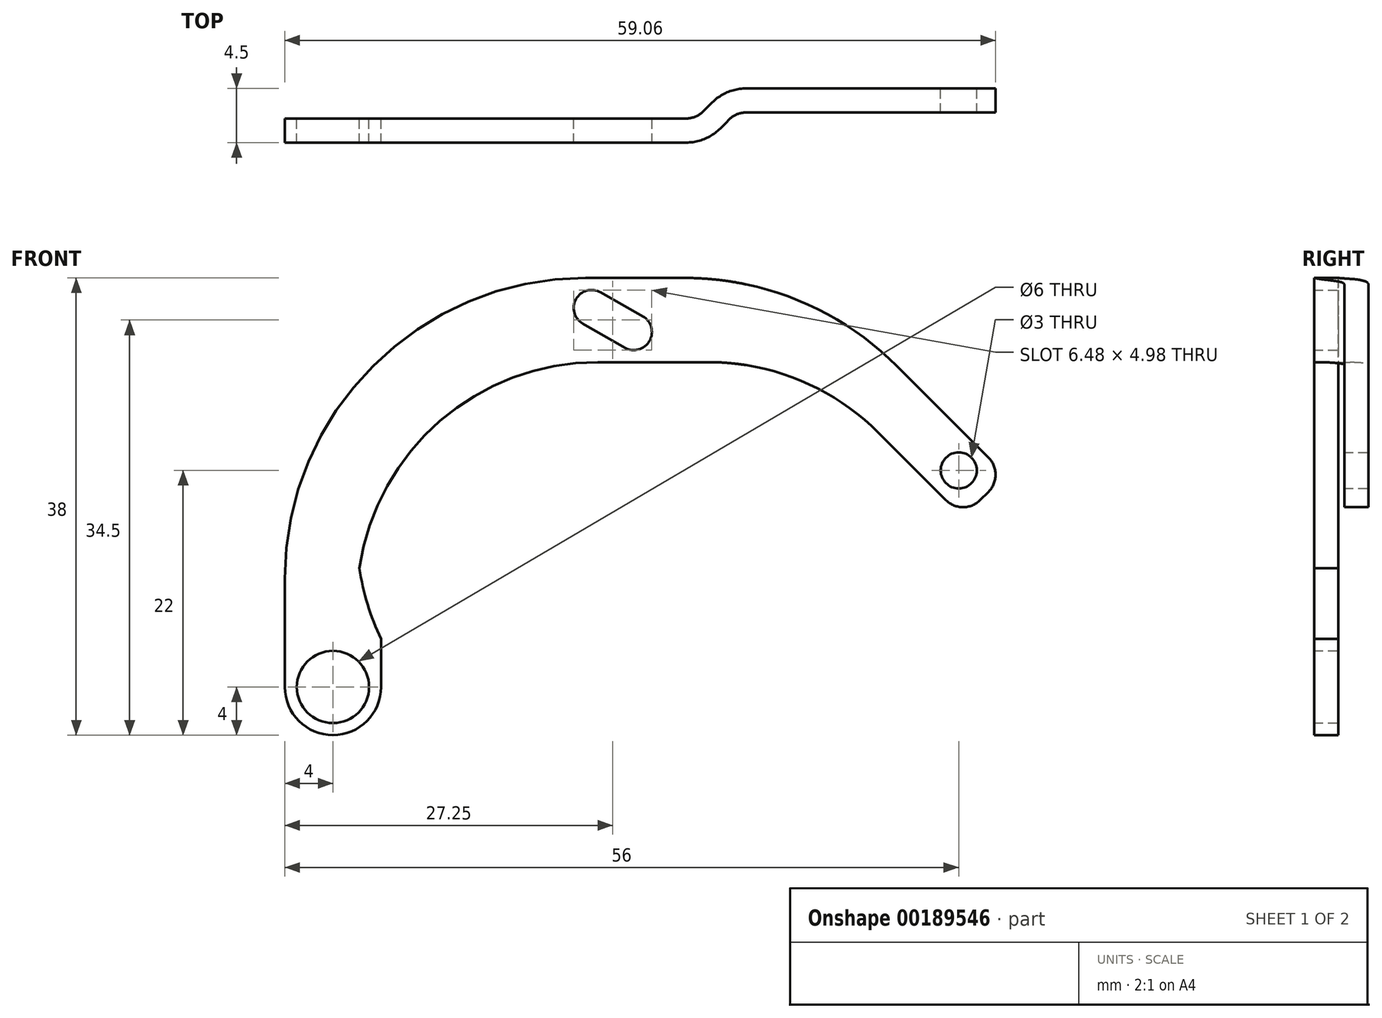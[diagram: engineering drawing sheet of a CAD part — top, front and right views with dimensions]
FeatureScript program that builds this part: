
annotation { "Feature Type Name" : "Feature", "Feature Type Description" : "" }
export const myFeature = defineFeature(function(context is Context, id is Id, definition is map)
    precondition{}
    {
        {
            var Q0;
            Q0=qCreatedBy(makeId("Front.planeOp"),FACE);
            var sketch = newSketch(context, id + "F0", { "sketchPlane" : qUnion([Q0])});
            skCircle(sketch, "E0", {"center": v(0, 0) * mm, "radius": 3 * mm});
            skArc(sketch, "E1", {"start": v(24.26, 28.2) * mm, "mid": v(26.3, 28.76) * mm, "end": v(25.74, 30.8) * mm});
            skLineSegment(sketch, "E2.bottom", {"start": v(-4, -4) * mm, "end": v(4, -4) * mm});
            skLineSegment(sketch, "E2.top", {"start": v(-4, 27) * mm, "end": v(4, 27) * mm});
            skLineSegment(sketch, "E2.left", {"start": v(-4, -4) * mm, "end": v(-4, 27) * mm});
            skLineSegment(sketch, "E2.right", {"start": v(4, -4) * mm, "end": v(4, 27) * mm});
            skLineSegment(sketch, "E3.bottom", {"start": v(-4, 27) * mm, "end": v(39.46, 27) * mm});
            skLineSegment(sketch, "E3.top", {"start": v(-4, 34) * mm, "end": v(39.54, 34) * mm});
            skLineSegment(sketch, "E3.left", {"start": v(-4, 27) * mm, "end": v(-4, 34) * mm});
            skCircle(sketch, "E4", {"center": v(52, 18) * mm, "radius": 1.5 * mm});
            skLineSegment(sketch, "E5.left", {"start": v(52.35, 14.11) * mm, "end": v(39.46, 27) * mm});
            skLineSegment(sketch, "E5.right", {"start": v(55.89, 17.65) * mm, "end": v(39.54, 34) * mm});
            skLineSegment(sketch, "E6.bottom", {"start": v(4, 27) * mm, "end": v(2, 27) * mm});
            skLineSegment(sketch, "E6.top", {"start": v(4, 4) * mm, "end": v(2, 4) * mm});
            skLineSegment(sketch, "E6.left", {"start": v(4, 27) * mm, "end": v(4, 4) * mm});
            skLineSegment(sketch, "E6.right", {"start": v(2, 27) * mm, "end": v(2, 4) * mm});
            skArc(sketch, "E7", {"start": v(22.24, 32.8) * mm, "mid": v(20.2, 32.24) * mm, "end": v(20.76, 30.2) * mm});
            skLineSegment(sketch, "E8", {"start": v(22.24, 32.8) * mm, "end": v(25.74, 30.8) * mm});
            skLineSegment(sketch, "E9", {"start": v(24.26, 28.2) * mm, "end": v(20.76, 30.2) * mm});
            skLineSegment(sketch, "E10", {"start": v(52.35, 14.11) * mm, "end": v(55.89, 17.65) * mm});
            skSolve(sketch);
        }
        {
            var Q0;
            Q0=makeQuery(id+"F0.imprint","IMPRINT",FACE,{"disambiguationData":[TD([[makeQuery(id+"F0.imprint","IMPRINT",EDGE,{"derivedFrom":sQuery(id+"F0.wireOp",EDGE,"E0")}),-1.0]])]});
            var Q1;
            Q1=makeQuery(id+"F0.imprint","IMPRINT",FACE,{"disambiguationData":[TD([[makeQuery(id+"F0.imprint","IMPRINT",EDGE,{"derivedFrom":sQuery(id+"F0.wireOp",EDGE,"E1")}),-1.0]])]});
            var Q2;
            Q2=makeQuery(id+"F0.imprint","IMPRINT",FACE,{"disambiguationData":[TD([[makeQuery(id+"F0.imprint","IMPRINT",EDGE,{"derivedFrom":sQuery(id+"F0.wireOp",EDGE,"J9uZ1ApI-m34T-gY4W-De5X-UlzJvXiWbMHB.bottom")}),-1.0]])]});
            var Q3;
            Q3=makeQuery(id+"F0.imprint","IMPRINT",FACE,{"disambiguationData":[TD([[makeQuery(id+"F0.imprint","IMPRINT",EDGE,{"derivedFrom":sQuery(id+"F0.wireOp",EDGE,"E4")}),-1.0]])]});
            extrude(context, id + "F1", {"entities" : qUnion([Q0, Q1, Q2, Q3]), "depth" : 4.5 * mm});
        }
        {
            var Q0;
            Q0=makeQuery(id+"F1.opExtrude","SWEPT_EDGE",EDGE,{"disambiguationData":[OSD([sQuery(id+"F0.wireOp",EDGE,"E3.bottom"),sQuery(id+"F0.wireOp",EDGE,"E5.left")])]});
            var Q1;
            Q1=makeQuery(id+"F1.opExtrude","SWEPT_EDGE",EDGE,{"disambiguationData":[OSD([sQuery(id+"F0.wireOp",EDGE,"E3.bottom"),sQuery(id+"F0.wireOp",EDGE,"E6.bottom"),sQuery(id+"F0.wireOp",EDGE,"E6.right")])]});
            fillet(context, id + "F2", {"entities" : qUnion([Q0, Q1]), "radius" : 20 * mm, "tangentPropagation" : true, "allowEdgeOverflow" : false});
        }
        {
            var Q0;
            Q0=makeQuery(id+"F1.opExtrude","SWEPT_EDGE",EDGE,{"disambiguationData":[OSD([sQuery(id+"F0.wireOp",EDGE,"E3.top"),sQuery(id+"F0.wireOp",EDGE,"E3.left")])]});
            fillet(context, id + "F3", {"entities" : qUnion([Q0]), "radius" : 25 * mm, "tangentPropagation" : true, "allowEdgeOverflow" : false});
        }
        {
            var Q0;
            Q0=makeQuery(id+"F1.opExtrude","SWEPT_EDGE",EDGE,{"disambiguationData":[OSD([sQuery(id+"F0.wireOp",EDGE,"E3.top"),sQuery(id+"F0.wireOp",EDGE,"E5.right")])]});
            fillet(context, id + "F4", {"entities" : qUnion([Q0]), "radius" : 25 * mm, "tangentPropagation" : true, "allowEdgeOverflow" : false});
        }
        {
            var Q0;
            Q0=makeQuery(id+"F1.opExtrude","SWEPT_EDGE",EDGE,{"disambiguationData":[OSD([sQuery(id+"F0.wireOp",EDGE,"E2.bottom"),sQuery(id+"F0.wireOp",EDGE,"E2.right")])]});
            var Q1;
            Q1=makeQuery(id+"F1.opExtrude","SWEPT_EDGE",EDGE,{"disambiguationData":[OSD([sQuery(id+"F0.wireOp",EDGE,"E2.bottom"),sQuery(id+"F0.wireOp",EDGE,"E2.left")])]});
            var Q2;
            Q2=makeQuery(id+"F1.opExtrude","SWEPT_EDGE",EDGE,{"disambiguationData":[OSD([sQuery(id+"F0.wireOp",EDGE,"E2.right"),sQuery(id+"F0.wireOp",EDGE,"E6.top"),sQuery(id+"F0.wireOp",EDGE,"E6.left")])]});
            fillet(context, id + "F5", {"entities" : qUnion([Q0, Q1, Q2]), "radius" : 4 * mm, "tangentPropagation" : true, "allowEdgeOverflow" : false});
        }
        {
            var Q0;
            Q0=makeQuery(id+"F2.opFillet","BLEND_EDGE",EDGE,{"blendedFrom":[makeQuery(id+"F1.opExtrude","SWEPT_EDGE",EDGE,{"disambiguationData":[OSD([sQuery(id+"F0.wireOp",EDGE,"J9uZ1ApI-m34T-gY4W-De5X-UlzJvXiWbMHB.top"),sQuery(id+"F0.wireOp",EDGE,"E5.top"),sQuery(id+"F0.wireOp",EDGE,"E5.left")])]}),makeQuery(id+"F1.opExtrude","SWEPT_FACE",FACE,{"disambiguationData":[OSD([sQuery(id+"F0.wireOp",EDGE,"E5.bottom")])]})],"blendedInto":[makeQuery(id+"F1.opExtrude","SWEPT_FACE",FACE,{"disambiguationData":[OSD([sQuery(id+"F0.wireOp",EDGE,"E5.bottom")])]})]});
            var Q1;
            Q1=makeQuery(id+"F4.opFillet","BLEND_EDGE",EDGE,{"blendedFrom":[makeQuery(id+"F1.opExtrude","SWEPT_EDGE",EDGE,{"disambiguationData":[OSD([sQuery(id+"F0.wireOp",EDGE,"J9uZ1ApI-m34T-gY4W-De5X-UlzJvXiWbMHB.bottom"),sQuery(id+"F0.wireOp",EDGE,"J9uZ1ApI-m34T-gY4W-De5X-UlzJvXiWbMHB.right")])]}),makeQuery(id+"F1.opExtrude","SWEPT_FACE",FACE,{"disambiguationData":[OSD([sQuery(id+"F0.wireOp",EDGE,"E5.bottom")])]})],"blendedInto":[makeQuery(id+"F1.opExtrude","SWEPT_FACE",FACE,{"disambiguationData":[OSD([sQuery(id+"F0.wireOp",EDGE,"E5.bottom")])]})]});
            var Q2;
            Q2=makeQuery(id+"F5.opFillet","BLEND_EDGE",EDGE,{"blendedFrom":[makeQuery(id+"F1.opExtrude","SWEPT_EDGE",EDGE,{"disambiguationData":[OSD([sQuery(id+"F0.wireOp",EDGE,"E2.right"),sQuery(id+"F0.wireOp",EDGE,"E6.top"),sQuery(id+"F0.wireOp",EDGE,"E6.left")])]}),makeQuery(id+"F1.opExtrude","SWEPT_FACE",FACE,{"disambiguationData":[OSD([sQuery(id+"F0.wireOp",EDGE,"E6.right")])]})],"blendedInto":[makeQuery(id+"F1.opExtrude","SWEPT_FACE",FACE,{"disambiguationData":[OSD([sQuery(id+"F0.wireOp",EDGE,"E6.right")])]})]});
            var Q3;
            Q3=makeQuery(id+"F1.opExtrude","SWEPT_EDGE",EDGE,{"disambiguationData":[OSD([sQuery(id+"F0.wireOp",EDGE,"E5.left"),sQuery(id+"F0.wireOp",EDGE,"E10")])]});
            var Q4;
            Q4=makeQuery(id+"F1.opExtrude","SWEPT_EDGE",EDGE,{"disambiguationData":[OSD([sQuery(id+"F0.wireOp",EDGE,"E5.right"),sQuery(id+"F0.wireOp",EDGE,"E10")])]});
            fillet(context, id + "F6", {"entities" : qUnion([Q0, Q1, Q2, Q3, Q4]), "radius" : 2 * mm, "tangentPropagation" : true, "allowEdgeOverflow" : false});
        }
        {
            var Q0;
            Q0=qCreatedBy(makeId("Top.planeOp"),FACE);
            var sketch = newSketch(context, id + "F7", { "sketchPlane" : qUnion([Q0])});
            skLineSegment(sketch, "E11.bottom", {"start": v(29.5, -6) * mm, "end": v(69.5, -6) * mm});
            skLineSegment(sketch, "E11.top", {"start": v(33.5, -2) * mm, "end": v(69.5, -2) * mm});
            skLineSegment(sketch, "E11.right", {"start": v(69.5, -6) * mm, "end": v(69.5, -2) * mm});
            skLineSegment(sketch, "E12.bottom", {"start": v(-25.82, 1.5) * mm, "end": v(34.18, 1.5) * mm});
            skLineSegment(sketch, "E12.top", {"start": v(-25.82, -2.5) * mm, "end": v(30.18, -2.5) * mm});
            skLineSegment(sketch, "E12.left", {"start": v(-25.82, 1.5) * mm, "end": v(-25.82, -2.5) * mm});
            skLineSegment(sketch, "E13", {"start": v(29.5, -6) * mm, "end": v(33.5, -2) * mm});
            skLineSegment(sketch, "E14", {"start": v(34.18, 1.5) * mm, "end": v(30.18, -2.5) * mm});
            skSolve(sketch);
        }
        {
            var Q0;
            Q0=makeQuery(id+"F7.imprint","IMPRINT",FACE,{"disambiguationData":[TD([[makeQuery(id+"F7.imprint","IMPRINT",EDGE,{"derivedFrom":sQuery(id+"F7.wireOp",EDGE,"E12.bottom")}),-1.0]])]});
            var Q1;
            Q1=makeQuery(id+"F7.imprint","IMPRINT",FACE,{"disambiguationData":[TD([[makeQuery(id+"F7.imprint","IMPRINT",EDGE,{"derivedFrom":sQuery(id+"F7.wireOp",EDGE,"E11.bottom")}),1.0]])]});
            extrude(context, id + "F8", {"entities" : qUnion([Q0, Q1]), "operationType" : NewBodyOperationType.REMOVE, "endBound" : BoundingType.SYMMETRIC, "depth" : 100 * mm});
        }
        {
            var Q0;
            Q0=makeQuery(id+"F8.boolean.opBoolean","COPY",EDGE,{"derivedFrom":makeQuery(id+"F8.opExtrude","SWEPT_EDGE",EDGE,{"disambiguationData":[OSD([sQuery(id+"F7.wireOp",EDGE,"E11.top"),sQuery(id+"F7.wireOp",EDGE,"E13")])]})});
            var Q1;
            Q1=makeQuery(id+"F8.boolean.opBoolean","COPY",EDGE,{"derivedFrom":makeQuery(id+"F8.opExtrude","SWEPT_EDGE",EDGE,{"disambiguationData":[OSD([sQuery(id+"F7.wireOp",EDGE,"E12.top"),sQuery(id+"F7.wireOp",EDGE,"E14")])]})});
            fillet(context, id + "F9", {"entities" : qUnion([Q0, Q1]), "radius" : 2 * mm, "tangentPropagation" : true, "allowEdgeOverflow" : false});
        }
        {
            var Q0;
            Q0=makeQuery(id+"F8.boolean.opBoolean","INTERSECT",EDGE,{"derivedFrom":[makeQuery(id+"F1.opExtrude","CAP_FACE",FACE,{"disambiguationData":[OSD([sQuery(id+"F0.wireOp",EDGE,"E0"),sQuery(id+"F0.wireOp",EDGE,"E1"),sQuery(id+"F0.wireOp",EDGE,"E2.bottom"),sQuery(id+"F0.wireOp",EDGE,"E2.left"),sQuery(id+"F0.wireOp",EDGE,"E2.right"),sQuery(id+"F0.wireOp",EDGE,"E3.bottom"),sQuery(id+"F0.wireOp",EDGE,"E3.top"),sQuery(id+"F0.wireOp",EDGE,"E3.left"),sQuery(id+"F0.wireOp",EDGE,"E4"),sQuery(id+"F0.wireOp",EDGE,"E5.left"),sQuery(id+"F0.wireOp",EDGE,"E5.right"),sQuery(id+"F0.wireOp",EDGE,"E6.bottom"),sQuery(id+"F0.wireOp",EDGE,"E6.top"),sQuery(id+"F0.wireOp",EDGE,"E6.right"),sQuery(id+"F0.wireOp",EDGE,"E7"),sQuery(id+"F0.wireOp",EDGE,"E8"),sQuery(id+"F0.wireOp",EDGE,"E9"),sQuery(id+"F0.wireOp",EDGE,"E10")])],"isStart":false}),makeQuery(id+"F8.opExtrude","SWEPT_FACE",FACE,{"disambiguationData":[OSD([sQuery(id+"F7.wireOp",EDGE,"E13")])]})]});
            var Q1;
            Q1=makeQuery(id+"F8.boolean.opBoolean","INTERSECT",EDGE,{"derivedFrom":[makeQuery(id+"F1.opExtrude","CAP_FACE",FACE,{"disambiguationData":[OSD([sQuery(id+"F0.wireOp",EDGE,"E0"),sQuery(id+"F0.wireOp",EDGE,"E1"),sQuery(id+"F0.wireOp",EDGE,"E2.bottom"),sQuery(id+"F0.wireOp",EDGE,"E2.left"),sQuery(id+"F0.wireOp",EDGE,"E2.right"),sQuery(id+"F0.wireOp",EDGE,"E3.bottom"),sQuery(id+"F0.wireOp",EDGE,"E3.top"),sQuery(id+"F0.wireOp",EDGE,"E3.left"),sQuery(id+"F0.wireOp",EDGE,"E4"),sQuery(id+"F0.wireOp",EDGE,"E5.left"),sQuery(id+"F0.wireOp",EDGE,"E5.right"),sQuery(id+"F0.wireOp",EDGE,"E6.bottom"),sQuery(id+"F0.wireOp",EDGE,"E6.top"),sQuery(id+"F0.wireOp",EDGE,"E6.right"),sQuery(id+"F0.wireOp",EDGE,"E7"),sQuery(id+"F0.wireOp",EDGE,"E8"),sQuery(id+"F0.wireOp",EDGE,"E9"),sQuery(id+"F0.wireOp",EDGE,"E10")])],"isStart":true}),makeQuery(id+"F8.opExtrude","SWEPT_FACE",FACE,{"disambiguationData":[OSD([sQuery(id+"F7.wireOp",EDGE,"E14")])]})]});
            fillet(context, id + "F10", {"entities" : qUnion([Q0, Q1]), "radius" : 4 * mm, "tangentPropagation" : true, "allowEdgeOverflow" : false});
        }
    });
